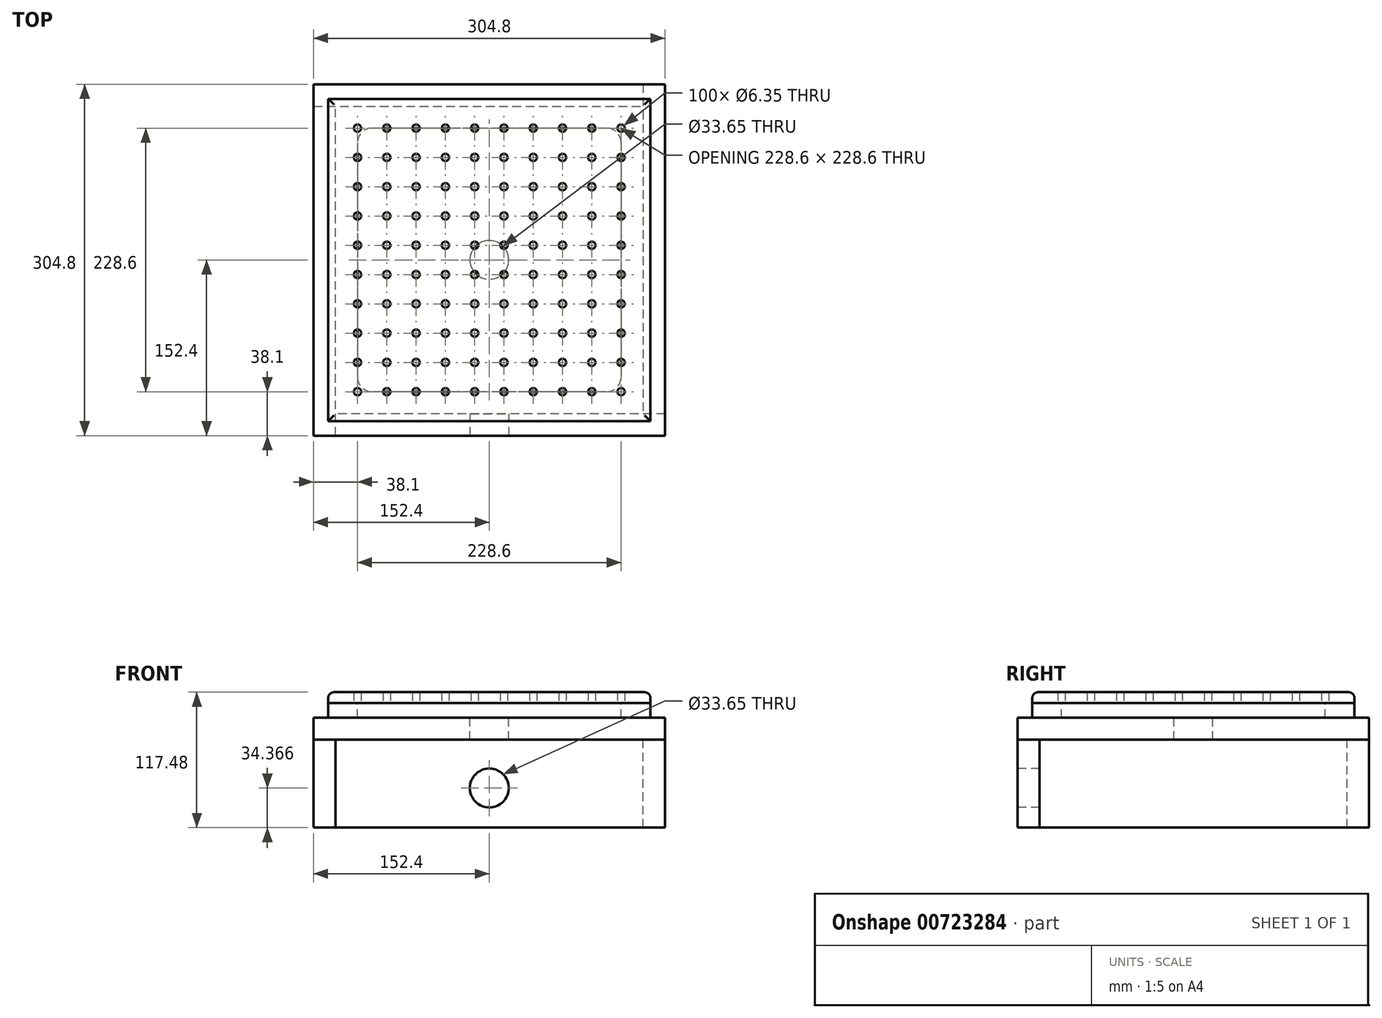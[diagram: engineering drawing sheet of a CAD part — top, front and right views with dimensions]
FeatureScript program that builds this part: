
annotation { "Feature Type Name" : "Feature", "Feature Type Description" : "" }
export const myFeature = defineFeature(function(context is Context, id is Id, definition is map)
    precondition{}
    {
        {
            var Q0;
            Q0=qCreatedBy(makeId("Top.planeOp"),FACE);
            var sketch = newSketch(context, id + "F0", { "sketchPlane" : qUnion([Q0])});
            skLineSegment(sketch, "E0.bottom", {"start": v(139.7, -139.7) * mm, "end": v(-139.7, -139.7) * mm});
            skLineSegment(sketch, "E0.top", {"start": v(139.7, 139.7) * mm, "end": v(-139.7, 139.7) * mm});
            skLineSegment(sketch, "E0.left", {"start": v(139.7, -139.7) * mm, "end": v(139.7, 139.7) * mm});
            skLineSegment(sketch, "E0.right", {"start": v(-139.7, -139.7) * mm, "end": v(-139.7, 139.7) * mm});
            skPoint(sketch, "E0.middle", {"position": v(0, 0) * mm});
            skCircle(sketch, "E1", {"center": v(-114.3, 114.3) * mm, "radius": 3.18 * mm});
            skCircle(sketch, "E2.0.1.0", {"center": v(-114.3, 88.9) * mm, "radius": 3.18 * mm});
            skCircle(sketch, "E2.0.2.0", {"center": v(-114.3, 63.5) * mm, "radius": 3.18 * mm});
            skCircle(sketch, "E2.0.3.0", {"center": v(-114.3, 38.1) * mm, "radius": 3.18 * mm});
            skCircle(sketch, "E2.0.4.0", {"center": v(-114.3, 12.7) * mm, "radius": 3.18 * mm});
            skCircle(sketch, "E2.0.5.0", {"center": v(-114.3, -12.7) * mm, "radius": 3.18 * mm});
            skCircle(sketch, "E2.0.6.0", {"center": v(-114.3, -38.1) * mm, "radius": 3.18 * mm});
            skCircle(sketch, "E2.0.7.0", {"center": v(-114.3, -63.5) * mm, "radius": 3.18 * mm});
            skCircle(sketch, "E2.0.8.0", {"center": v(-114.3, -88.9) * mm, "radius": 3.18 * mm});
            skCircle(sketch, "E2.0.9.0", {"center": v(-114.3, -114.3) * mm, "radius": 3.18 * mm});
            skCircle(sketch, "E2.1.0.0", {"center": v(-88.9, 114.3) * mm, "radius": 3.18 * mm});
            skCircle(sketch, "E2.1.1.0", {"center": v(-88.9, 88.9) * mm, "radius": 3.18 * mm});
            skCircle(sketch, "E2.1.2.0", {"center": v(-88.9, 63.5) * mm, "radius": 3.18 * mm});
            skCircle(sketch, "E2.1.3.0", {"center": v(-88.9, 38.1) * mm, "radius": 3.18 * mm});
            skCircle(sketch, "E2.1.4.0", {"center": v(-88.9, 12.7) * mm, "radius": 3.18 * mm});
            skCircle(sketch, "E2.1.5.0", {"center": v(-88.9, -12.7) * mm, "radius": 3.18 * mm});
            skCircle(sketch, "E2.1.6.0", {"center": v(-88.9, -38.1) * mm, "radius": 3.18 * mm});
            skCircle(sketch, "E2.1.7.0", {"center": v(-88.9, -63.5) * mm, "radius": 3.18 * mm});
            skCircle(sketch, "E2.1.8.0", {"center": v(-88.9, -88.9) * mm, "radius": 3.18 * mm});
            skCircle(sketch, "E2.1.9.0", {"center": v(-88.9, -114.3) * mm, "radius": 3.18 * mm});
            skCircle(sketch, "E2.2.0.0", {"center": v(-63.5, 114.3) * mm, "radius": 3.18 * mm});
            skCircle(sketch, "E2.2.1.0", {"center": v(-63.5, 88.9) * mm, "radius": 3.18 * mm});
            skCircle(sketch, "E2.2.2.0", {"center": v(-63.5, 63.5) * mm, "radius": 3.18 * mm});
            skCircle(sketch, "E2.2.3.0", {"center": v(-63.5, 38.1) * mm, "radius": 3.18 * mm});
            skCircle(sketch, "E2.2.4.0", {"center": v(-63.5, 12.7) * mm, "radius": 3.18 * mm});
            skCircle(sketch, "E2.2.5.0", {"center": v(-63.5, -12.7) * mm, "radius": 3.18 * mm});
            skCircle(sketch, "E2.2.6.0", {"center": v(-63.5, -38.1) * mm, "radius": 3.18 * mm});
            skCircle(sketch, "E2.2.7.0", {"center": v(-63.5, -63.5) * mm, "radius": 3.18 * mm});
            skCircle(sketch, "E2.2.8.0", {"center": v(-63.5, -88.9) * mm, "radius": 3.18 * mm});
            skCircle(sketch, "E2.2.9.0", {"center": v(-63.5, -114.3) * mm, "radius": 3.18 * mm});
            skCircle(sketch, "E2.3.0.0", {"center": v(-38.1, 114.3) * mm, "radius": 3.18 * mm});
            skCircle(sketch, "E2.3.1.0", {"center": v(-38.1, 88.9) * mm, "radius": 3.18 * mm});
            skCircle(sketch, "E2.3.2.0", {"center": v(-38.1, 63.5) * mm, "radius": 3.18 * mm});
            skCircle(sketch, "E2.3.3.0", {"center": v(-38.1, 38.1) * mm, "radius": 3.18 * mm});
            skCircle(sketch, "E2.3.4.0", {"center": v(-38.1, 12.7) * mm, "radius": 3.18 * mm});
            skCircle(sketch, "E2.3.5.0", {"center": v(-38.1, -12.7) * mm, "radius": 3.18 * mm});
            skCircle(sketch, "E2.3.6.0", {"center": v(-38.1, -38.1) * mm, "radius": 3.18 * mm});
            skCircle(sketch, "E2.3.7.0", {"center": v(-38.1, -63.5) * mm, "radius": 3.18 * mm});
            skCircle(sketch, "E2.3.8.0", {"center": v(-38.1, -88.9) * mm, "radius": 3.18 * mm});
            skCircle(sketch, "E2.3.9.0", {"center": v(-38.1, -114.3) * mm, "radius": 3.18 * mm});
            skCircle(sketch, "E2.4.0.0", {"center": v(-12.7, 114.3) * mm, "radius": 3.18 * mm});
            skCircle(sketch, "E2.4.1.0", {"center": v(-12.7, 88.9) * mm, "radius": 3.18 * mm});
            skCircle(sketch, "E2.4.2.0", {"center": v(-12.7, 63.5) * mm, "radius": 3.18 * mm});
            skCircle(sketch, "E2.4.3.0", {"center": v(-12.7, 38.1) * mm, "radius": 3.18 * mm});
            skCircle(sketch, "E2.4.4.0", {"center": v(-12.7, 12.7) * mm, "radius": 3.18 * mm});
            skCircle(sketch, "E2.4.5.0", {"center": v(-12.7, -12.7) * mm, "radius": 3.18 * mm});
            skCircle(sketch, "E2.4.6.0", {"center": v(-12.7, -38.1) * mm, "radius": 3.18 * mm});
            skCircle(sketch, "E2.4.7.0", {"center": v(-12.7, -63.5) * mm, "radius": 3.18 * mm});
            skCircle(sketch, "E2.4.8.0", {"center": v(-12.7, -88.9) * mm, "radius": 3.18 * mm});
            skCircle(sketch, "E2.4.9.0", {"center": v(-12.7, -114.3) * mm, "radius": 3.18 * mm});
            skCircle(sketch, "E2.5.0.0", {"center": v(12.7, 114.3) * mm, "radius": 3.18 * mm});
            skCircle(sketch, "E2.5.1.0", {"center": v(12.7, 88.9) * mm, "radius": 3.18 * mm});
            skCircle(sketch, "E2.5.2.0", {"center": v(12.7, 63.5) * mm, "radius": 3.18 * mm});
            skCircle(sketch, "E2.5.3.0", {"center": v(12.7, 38.1) * mm, "radius": 3.18 * mm});
            skCircle(sketch, "E2.5.4.0", {"center": v(12.7, 12.7) * mm, "radius": 3.18 * mm});
            skCircle(sketch, "E2.5.5.0", {"center": v(12.7, -12.7) * mm, "radius": 3.18 * mm});
            skCircle(sketch, "E2.5.6.0", {"center": v(12.7, -38.1) * mm, "radius": 3.18 * mm});
            skCircle(sketch, "E2.5.7.0", {"center": v(12.7, -63.5) * mm, "radius": 3.18 * mm});
            skCircle(sketch, "E2.5.8.0", {"center": v(12.7, -88.9) * mm, "radius": 3.18 * mm});
            skCircle(sketch, "E2.5.9.0", {"center": v(12.7, -114.3) * mm, "radius": 3.18 * mm});
            skCircle(sketch, "E2.6.0.0", {"center": v(38.1, 114.3) * mm, "radius": 3.18 * mm});
            skCircle(sketch, "E2.6.1.0", {"center": v(38.1, 88.9) * mm, "radius": 3.18 * mm});
            skCircle(sketch, "E2.6.2.0", {"center": v(38.1, 63.5) * mm, "radius": 3.18 * mm});
            skCircle(sketch, "E2.6.3.0", {"center": v(38.1, 38.1) * mm, "radius": 3.18 * mm});
            skCircle(sketch, "E2.6.4.0", {"center": v(38.1, 12.7) * mm, "radius": 3.18 * mm});
            skCircle(sketch, "E2.6.5.0", {"center": v(38.1, -12.7) * mm, "radius": 3.18 * mm});
            skCircle(sketch, "E2.6.6.0", {"center": v(38.1, -38.1) * mm, "radius": 3.18 * mm});
            skCircle(sketch, "E2.6.7.0", {"center": v(38.1, -63.5) * mm, "radius": 3.18 * mm});
            skCircle(sketch, "E2.6.8.0", {"center": v(38.1, -88.9) * mm, "radius": 3.18 * mm});
            skCircle(sketch, "E2.6.9.0", {"center": v(38.1, -114.3) * mm, "radius": 3.18 * mm});
            skCircle(sketch, "E2.7.0.0", {"center": v(63.5, 114.3) * mm, "radius": 3.18 * mm});
            skCircle(sketch, "E2.7.1.0", {"center": v(63.5, 88.9) * mm, "radius": 3.18 * mm});
            skCircle(sketch, "E2.7.2.0", {"center": v(63.5, 63.5) * mm, "radius": 3.18 * mm});
            skCircle(sketch, "E2.7.3.0", {"center": v(63.5, 38.1) * mm, "radius": 3.18 * mm});
            skCircle(sketch, "E2.7.4.0", {"center": v(63.5, 12.7) * mm, "radius": 3.18 * mm});
            skCircle(sketch, "E2.7.5.0", {"center": v(63.5, -12.7) * mm, "radius": 3.18 * mm});
            skCircle(sketch, "E2.7.6.0", {"center": v(63.5, -38.1) * mm, "radius": 3.18 * mm});
            skCircle(sketch, "E2.7.7.0", {"center": v(63.5, -63.5) * mm, "radius": 3.18 * mm});
            skCircle(sketch, "E2.7.8.0", {"center": v(63.5, -88.9) * mm, "radius": 3.18 * mm});
            skCircle(sketch, "E2.7.9.0", {"center": v(63.5, -114.3) * mm, "radius": 3.18 * mm});
            skCircle(sketch, "E2.8.0.0", {"center": v(88.9, 114.3) * mm, "radius": 3.18 * mm});
            skCircle(sketch, "E2.8.1.0", {"center": v(88.9, 88.9) * mm, "radius": 3.18 * mm});
            skCircle(sketch, "E2.8.2.0", {"center": v(88.9, 63.5) * mm, "radius": 3.18 * mm});
            skCircle(sketch, "E2.8.3.0", {"center": v(88.9, 38.1) * mm, "radius": 3.18 * mm});
            skCircle(sketch, "E2.8.4.0", {"center": v(88.9, 12.7) * mm, "radius": 3.18 * mm});
            skCircle(sketch, "E2.8.5.0", {"center": v(88.9, -12.7) * mm, "radius": 3.18 * mm});
            skCircle(sketch, "E2.8.6.0", {"center": v(88.9, -38.1) * mm, "radius": 3.18 * mm});
            skCircle(sketch, "E2.8.7.0", {"center": v(88.9, -63.5) * mm, "radius": 3.18 * mm});
            skCircle(sketch, "E2.8.8.0", {"center": v(88.9, -88.9) * mm, "radius": 3.18 * mm});
            skCircle(sketch, "E2.8.9.0", {"center": v(88.9, -114.3) * mm, "radius": 3.18 * mm});
            skCircle(sketch, "E2.9.0.0", {"center": v(114.3, 114.3) * mm, "radius": 3.18 * mm});
            skCircle(sketch, "E2.9.1.0", {"center": v(114.3, 88.9) * mm, "radius": 3.18 * mm});
            skCircle(sketch, "E2.9.2.0", {"center": v(114.3, 63.5) * mm, "radius": 3.18 * mm});
            skCircle(sketch, "E2.9.3.0", {"center": v(114.3, 38.1) * mm, "radius": 3.18 * mm});
            skCircle(sketch, "E2.9.4.0", {"center": v(114.3, 12.7) * mm, "radius": 3.18 * mm});
            skCircle(sketch, "E2.9.5.0", {"center": v(114.3, -12.7) * mm, "radius": 3.18 * mm});
            skCircle(sketch, "E2.9.6.0", {"center": v(114.3, -38.1) * mm, "radius": 3.18 * mm});
            skCircle(sketch, "E2.9.7.0", {"center": v(114.3, -63.5) * mm, "radius": 3.18 * mm});
            skCircle(sketch, "E2.9.8.0", {"center": v(114.3, -88.9) * mm, "radius": 3.18 * mm});
            skCircle(sketch, "E2.9.9.0", {"center": v(114.3, -114.3) * mm, "radius": 3.18 * mm});
            skLineSegment(sketch, "E2.direction1", {"start": v(-114.3, 114.3) * mm, "end": v(-88.9, 114.3) * mm, "construction": true});
            skLineSegment(sketch, "E2.direction2", {"start": v(-114.3, 114.3) * mm, "end": v(-114.3, 88.9) * mm, "construction": true});
            skSolve(sketch);
        }
        {
            var Q0;
            Q0=makeQuery(id+"F0.imprint","IMPRINT",FACE,{"disambiguationData":[TD([[makeQuery(id+"F0.imprint","IMPRINT",EDGE,{"derivedFrom":sQuery(id+"F0.wireOp",EDGE,"E0.bottom")}),-1.0]])]});
            extrude(context, id + "F1", {"entities" : qUnion([Q0]), "depth" : 9.52 * mm, "offsetDistance" : 25.4 * mm});
        }
        {
            var Q0;
            Q0=makeQuery(id+"F1.opExtrude","CAP_EDGE",EDGE,{"disambiguationData":[OSD([sQuery(id+"F0.wireOp",EDGE,"E0.right")])],"isStart":false});
            var Q1;
            Q1=makeQuery(id+"F1.opExtrude","CAP_EDGE",EDGE,{"disambiguationData":[OSD([sQuery(id+"F0.wireOp",EDGE,"E0.left")])],"isStart":false});
            var Q2;
            Q2=makeQuery(id+"F1.opExtrude","CAP_EDGE",EDGE,{"disambiguationData":[OSD([sQuery(id+"F0.wireOp",EDGE,"E0.top")])],"isStart":false});
            var Q3;
            Q3=makeQuery(id+"F1.opExtrude","CAP_EDGE",EDGE,{"disambiguationData":[OSD([sQuery(id+"F0.wireOp",EDGE,"E0.bottom")])],"isStart":false});
            fillet(context, id + "F2", {"entities" : qUnion([Q0, Q1, Q2, Q3]), "radius" : 5.08 * mm, "tangentPropagation" : true, "allowEdgeOverflow" : false});
        }
        {
            var Q0;
            Q0=makeQuery(id+"F1.opExtrude","CAP_FACE",FACE,{"disambiguationData":[OSD([sQuery(id+"F0.wireOp",EDGE,"E0.bottom"),sQuery(id+"F0.wireOp",EDGE,"E0.top"),sQuery(id+"F0.wireOp",EDGE,"E0.left"),sQuery(id+"F0.wireOp",EDGE,"E0.right"),sQuery(id+"F0.wireOp",EDGE,"E1"),sQuery(id+"F0.wireOp",EDGE,"E2.0.1.0"),sQuery(id+"F0.wireOp",EDGE,"E2.0.2.0"),sQuery(id+"F0.wireOp",EDGE,"E2.0.3.0"),sQuery(id+"F0.wireOp",EDGE,"E2.0.4.0"),sQuery(id+"F0.wireOp",EDGE,"E2.0.5.0"),sQuery(id+"F0.wireOp",EDGE,"E2.0.6.0"),sQuery(id+"F0.wireOp",EDGE,"E2.0.7.0"),sQuery(id+"F0.wireOp",EDGE,"E2.0.8.0"),sQuery(id+"F0.wireOp",EDGE,"E2.0.9.0"),sQuery(id+"F0.wireOp",EDGE,"E2.0.10.0"),sQuery(id+"F0.wireOp",EDGE,"E2.1.0.0"),sQuery(id+"F0.wireOp",EDGE,"E2.1.1.0"),sQuery(id+"F0.wireOp",EDGE,"E2.1.2.0"),sQuery(id+"F0.wireOp",EDGE,"E2.1.3.0"),sQuery(id+"F0.wireOp",EDGE,"E2.1.4.0"),sQuery(id+"F0.wireOp",EDGE,"E2.1.5.0"),sQuery(id+"F0.wireOp",EDGE,"E2.1.6.0"),sQuery(id+"F0.wireOp",EDGE,"E2.1.7.0"),sQuery(id+"F0.wireOp",EDGE,"E2.1.8.0"),sQuery(id+"F0.wireOp",EDGE,"E2.1.9.0"),sQuery(id+"F0.wireOp",EDGE,"E2.1.10.0"),sQuery(id+"F0.wireOp",EDGE,"E2.2.0.0"),sQuery(id+"F0.wireOp",EDGE,"E2.2.1.0"),sQuery(id+"F0.wireOp",EDGE,"E2.2.2.0"),sQuery(id+"F0.wireOp",EDGE,"E2.2.3.0"),sQuery(id+"F0.wireOp",EDGE,"E2.2.4.0"),sQuery(id+"F0.wireOp",EDGE,"E2.2.5.0"),sQuery(id+"F0.wireOp",EDGE,"E2.2.6.0"),sQuery(id+"F0.wireOp",EDGE,"E2.2.7.0"),sQuery(id+"F0.wireOp",EDGE,"E2.2.8.0"),sQuery(id+"F0.wireOp",EDGE,"E2.2.9.0"),sQuery(id+"F0.wireOp",EDGE,"E2.2.10.0"),sQuery(id+"F0.wireOp",EDGE,"E2.3.0.0"),sQuery(id+"F0.wireOp",EDGE,"E2.3.1.0"),sQuery(id+"F0.wireOp",EDGE,"E2.3.2.0"),sQuery(id+"F0.wireOp",EDGE,"E2.3.3.0"),sQuery(id+"F0.wireOp",EDGE,"E2.3.4.0"),sQuery(id+"F0.wireOp",EDGE,"E2.3.5.0"),sQuery(id+"F0.wireOp",EDGE,"E2.3.6.0"),sQuery(id+"F0.wireOp",EDGE,"E2.3.7.0"),sQuery(id+"F0.wireOp",EDGE,"E2.3.8.0"),sQuery(id+"F0.wireOp",EDGE,"E2.3.9.0"),sQuery(id+"F0.wireOp",EDGE,"E2.3.10.0"),sQuery(id+"F0.wireOp",EDGE,"E2.4.0.0"),sQuery(id+"F0.wireOp",EDGE,"E2.4.1.0"),sQuery(id+"F0.wireOp",EDGE,"E2.4.2.0"),sQuery(id+"F0.wireOp",EDGE,"E2.4.3.0"),sQuery(id+"F0.wireOp",EDGE,"E2.4.4.0"),sQuery(id+"F0.wireOp",EDGE,"E2.4.5.0"),sQuery(id+"F0.wireOp",EDGE,"E2.4.6.0"),sQuery(id+"F0.wireOp",EDGE,"E2.4.7.0"),sQuery(id+"F0.wireOp",EDGE,"E2.4.8.0"),sQuery(id+"F0.wireOp",EDGE,"E2.4.9.0"),sQuery(id+"F0.wireOp",EDGE,"E2.4.10.0"),sQuery(id+"F0.wireOp",EDGE,"E2.5.0.0"),sQuery(id+"F0.wireOp",EDGE,"E2.5.1.0"),sQuery(id+"F0.wireOp",EDGE,"E2.5.2.0"),sQuery(id+"F0.wireOp",EDGE,"E2.5.3.0"),sQuery(id+"F0.wireOp",EDGE,"E2.5.4.0"),sQuery(id+"F0.wireOp",EDGE,"E2.5.5.0"),sQuery(id+"F0.wireOp",EDGE,"E2.5.6.0"),sQuery(id+"F0.wireOp",EDGE,"E2.5.7.0"),sQuery(id+"F0.wireOp",EDGE,"E2.5.8.0"),sQuery(id+"F0.wireOp",EDGE,"E2.5.9.0"),sQuery(id+"F0.wireOp",EDGE,"E2.5.10.0"),sQuery(id+"F0.wireOp",EDGE,"E2.6.0.0"),sQuery(id+"F0.wireOp",EDGE,"E2.6.1.0"),sQuery(id+"F0.wireOp",EDGE,"E2.6.2.0"),sQuery(id+"F0.wireOp",EDGE,"E2.6.3.0"),sQuery(id+"F0.wireOp",EDGE,"E2.6.4.0"),sQuery(id+"F0.wireOp",EDGE,"E2.6.5.0"),sQuery(id+"F0.wireOp",EDGE,"E2.6.6.0"),sQuery(id+"F0.wireOp",EDGE,"E2.6.7.0"),sQuery(id+"F0.wireOp",EDGE,"E2.6.8.0"),sQuery(id+"F0.wireOp",EDGE,"E2.6.9.0"),sQuery(id+"F0.wireOp",EDGE,"E2.6.10.0"),sQuery(id+"F0.wireOp",EDGE,"E2.7.0.0"),sQuery(id+"F0.wireOp",EDGE,"E2.7.1.0"),sQuery(id+"F0.wireOp",EDGE,"E2.7.2.0"),sQuery(id+"F0.wireOp",EDGE,"E2.7.3.0"),sQuery(id+"F0.wireOp",EDGE,"E2.7.4.0"),sQuery(id+"F0.wireOp",EDGE,"E2.7.5.0"),sQuery(id+"F0.wireOp",EDGE,"E2.7.6.0"),sQuery(id+"F0.wireOp",EDGE,"E2.7.7.0"),sQuery(id+"F0.wireOp",EDGE,"E2.7.8.0"),sQuery(id+"F0.wireOp",EDGE,"E2.7.9.0"),sQuery(id+"F0.wireOp",EDGE,"E2.7.10.0"),sQuery(id+"F0.wireOp",EDGE,"E2.8.0.0"),sQuery(id+"F0.wireOp",EDGE,"E2.8.1.0"),sQuery(id+"F0.wireOp",EDGE,"E2.8.2.0"),sQuery(id+"F0.wireOp",EDGE,"E2.8.3.0"),sQuery(id+"F0.wireOp",EDGE,"E2.8.4.0"),sQuery(id+"F0.wireOp",EDGE,"E2.8.5.0"),sQuery(id+"F0.wireOp",EDGE,"E2.8.6.0"),sQuery(id+"F0.wireOp",EDGE,"E2.8.7.0"),sQuery(id+"F0.wireOp",EDGE,"E2.8.8.0"),sQuery(id+"F0.wireOp",EDGE,"E2.8.9.0"),sQuery(id+"F0.wireOp",EDGE,"E2.8.10.0"),sQuery(id+"F0.wireOp",EDGE,"E2.9.0.0"),sQuery(id+"F0.wireOp",EDGE,"E2.9.1.0"),sQuery(id+"F0.wireOp",EDGE,"E2.9.2.0"),sQuery(id+"F0.wireOp",EDGE,"E2.9.3.0"),sQuery(id+"F0.wireOp",EDGE,"E2.9.4.0"),sQuery(id+"F0.wireOp",EDGE,"E2.9.5.0"),sQuery(id+"F0.wireOp",EDGE,"E2.9.6.0"),sQuery(id+"F0.wireOp",EDGE,"E2.9.7.0"),sQuery(id+"F0.wireOp",EDGE,"E2.9.8.0"),sQuery(id+"F0.wireOp",EDGE,"E2.9.9.0"),sQuery(id+"F0.wireOp",EDGE,"E2.9.10.0"),sQuery(id+"F0.wireOp",EDGE,"E2.10.0.0"),sQuery(id+"F0.wireOp",EDGE,"E2.10.1.0"),sQuery(id+"F0.wireOp",EDGE,"E2.10.2.0"),sQuery(id+"F0.wireOp",EDGE,"E2.10.3.0"),sQuery(id+"F0.wireOp",EDGE,"E2.10.4.0"),sQuery(id+"F0.wireOp",EDGE,"E2.10.5.0"),sQuery(id+"F0.wireOp",EDGE,"E2.10.6.0"),sQuery(id+"F0.wireOp",EDGE,"E2.10.7.0"),sQuery(id+"F0.wireOp",EDGE,"E2.10.8.0"),sQuery(id+"F0.wireOp",EDGE,"E2.10.9.0"),sQuery(id+"F0.wireOp",EDGE,"E2.10.10.0")])],"isStart":true});
            var sketch = newSketch(context, id + "F3", { "sketchPlane" : qUnion([Q0])});
            skLineSegment(sketch, "E3.bottom", {"start": v(-139.7, 139.7) * mm, "end": v(139.7, 139.7) * mm});
            skLineSegment(sketch, "E3.top", {"start": v(-139.7, -139.7) * mm, "end": v(139.7, -139.7) * mm});
            skLineSegment(sketch, "E3.left", {"start": v(-139.7, 139.7) * mm, "end": v(-139.7, -139.7) * mm});
            skLineSegment(sketch, "E3.right", {"start": v(139.7, 139.7) * mm, "end": v(139.7, -139.7) * mm});
            skLineSegment(sketch, "E4.bottom", {"start": v(114.3, -114.3) * mm, "end": v(-114.3, -114.3) * mm});
            skLineSegment(sketch, "E4.top", {"start": v(114.3, 114.3) * mm, "end": v(-114.3, 114.3) * mm});
            skLineSegment(sketch, "E4.left", {"start": v(114.3, -114.3) * mm, "end": v(114.3, 114.3) * mm});
            skLineSegment(sketch, "E4.right", {"start": v(-114.3, -114.3) * mm, "end": v(-114.3, 114.3) * mm});
            skPoint(sketch, "E4.middle", {"position": v(0, 0) * mm});
            skSolve(sketch);
        }
        {
            var Q0;
            Q0 = qSketchRegion(id + "F3", true);
            extrude(context, id + "F4", {"entities" : qUnion([Q0]), "depth" : 12.7 * mm, "offsetDistance" : 25.4 * mm});
        }
        {
            var Q0;
            Q0=makeQuery(id+"F4.opExtrude","SWEPT_EDGE",EDGE,{"disambiguationData":[OSD([sQuery(id+"F3.wireOp",EDGE,"E4.top"),sQuery(id+"F3.wireOp",EDGE,"E4.right")])]});
            var Q1;
            Q1=makeQuery(id+"F4.opExtrude","SWEPT_EDGE",EDGE,{"disambiguationData":[OSD([sQuery(id+"F3.wireOp",EDGE,"E4.top"),sQuery(id+"F3.wireOp",EDGE,"E4.left")])]});
            var Q2;
            Q2=makeQuery(id+"F4.opExtrude","SWEPT_EDGE",EDGE,{"disambiguationData":[OSD([sQuery(id+"F3.wireOp",EDGE,"E4.bottom"),sQuery(id+"F3.wireOp",EDGE,"E4.left")])]});
            var Q3;
            Q3=makeQuery(id+"F4.opExtrude","SWEPT_EDGE",EDGE,{"disambiguationData":[OSD([sQuery(id+"F3.wireOp",EDGE,"E4.bottom"),sQuery(id+"F3.wireOp",EDGE,"E4.right")])]});
            fillet(context, id + "F5", {"entities" : qUnion([Q0, Q1, Q2, Q3]), "radius" : 12.7 * mm, "tangentPropagation" : true, "allowEdgeOverflow" : false});
        }
        {
            var Q0;
            Q0=makeQuery(id+"F4.opExtrude","CAP_FACE",FACE,{"disambiguationData":[OSD([sQuery(id+"F3.wireOp",EDGE,"E3.bottom"),sQuery(id+"F3.wireOp",EDGE,"E3.top"),sQuery(id+"F3.wireOp",EDGE,"E3.left"),sQuery(id+"F3.wireOp",EDGE,"E3.right"),sQuery(id+"F3.wireOp",EDGE,"E4.bottom"),sQuery(id+"F3.wireOp",EDGE,"E4.top"),sQuery(id+"F3.wireOp",EDGE,"E4.left"),sQuery(id+"F3.wireOp",EDGE,"E4.right")])],"isStart":false});
            var sketch = newSketch(context, id + "F6", { "sketchPlane" : qUnion([Q0])});
            skLineSegment(sketch, "E5.bottom", {"start": v(152.4, -152.4) * mm, "end": v(-152.4, -152.4) * mm});
            skLineSegment(sketch, "E5.top", {"start": v(152.4, 152.4) * mm, "end": v(-152.4, 152.4) * mm});
            skLineSegment(sketch, "E5.left", {"start": v(152.4, -152.4) * mm, "end": v(152.4, 152.4) * mm});
            skLineSegment(sketch, "E5.right", {"start": v(-152.4, -152.4) * mm, "end": v(-152.4, 152.4) * mm});
            skPoint(sketch, "E5.middle", {"position": v(0, 0) * mm});
            skCircle(sketch, "E6", {"center": v(0, 0) * mm, "radius": 16.83 * mm});
            skSolve(sketch);
        }
        {
            var Q0;
            Q0 = qSketchRegion(id + "F6", true);
            extrude(context, id + "F7", {"entities" : qUnion([Q0]), "depth" : 19.05 * mm, "offsetDistance" : 25.4 * mm});
        }
        {
            var Q0;
            Q0=makeQuery(id+"F7.opExtrude","CAP_FACE",FACE,{"disambiguationData":[OSD([sQuery(id+"F6.wireOp",EDGE,"E5.bottom"),sQuery(id+"F6.wireOp",EDGE,"E5.top"),sQuery(id+"F6.wireOp",EDGE,"E5.left"),sQuery(id+"F6.wireOp",EDGE,"E5.right"),sQuery(id+"F6.wireOp",EDGE,"E6")])],"isStart":false});
            var sketch = newSketch(context, id + "F8", { "sketchPlane" : qUnion([Q0])});
            skLineSegment(sketch, "E7.bottom", {"start": v(-152.4, 152.4) * mm, "end": v(-133.35, 152.4) * mm});
            skLineSegment(sketch, "E7.top", {"start": v(-152.4, -133.35) * mm, "end": v(-133.35, -133.35) * mm});
            skLineSegment(sketch, "E7.left", {"start": v(-152.4, 152.4) * mm, "end": v(-152.4, -133.35) * mm});
            skLineSegment(sketch, "E7.right", {"start": v(-133.35, 152.4) * mm, "end": v(-133.35, -133.35) * mm});
            skSolve(sketch);
        }
        {
            var Q0;
            Q0=makeQuery(id+"F8.imprint","IMPRINT",FACE,{"disambiguationData":[TD([[makeQuery(id+"F8.imprint","IMPRINT",EDGE,{"derivedFrom":sQuery(id+"F8.wireOp",EDGE,"E7.bottom")}),1.0]])]});
            extrude(context, id + "F9", {"entities" : qUnion([Q0]), "depth" : 76.2 * mm, "offsetDistance" : 25.4 * mm});
        }
        {
            var Q0;
            Q0=makeQuery(id+"F9.opExtrude","SWEPT_BODY",BODY,{"disambiguationData":[OSD([sQuery(id+"F8.wireOp",EDGE,"E7.bottom"),sQuery(id+"F8.wireOp",EDGE,"E7.top"),sQuery(id+"F8.wireOp",EDGE,"E7.left"),sQuery(id+"F8.wireOp",EDGE,"E7.right")])]});
            var Q1;
            Q1=makeQuery(id+"F7.opExtrude","CAP_EDGE",EDGE,{"disambiguationData":[OSD([sQuery(id+"F6.wireOp",EDGE,"E6")])],"isStart":false});
            circularPattern(context, id + "F10", {"entities" : qUnion([Q0]), "axis" : qUnion([Q1]), "angle" : 360 * degree, "instanceCount" : 4, "equalSpace" : true});
        }
        {
            var Q0;
            Q0=makeQuery(id+"F10.opPattern","COPY",FACE,{"derivedFrom":makeQuery(id+"F9.opExtrude","SWEPT_FACE",FACE,{"disambiguationData":[OSD([sQuery(id+"F8.wireOp",EDGE,"E7.left")])]}),"instanceName":"3"});
            var sketch = newSketch(context, id + "F11", { "sketchPlane" : qUnion([Q0])});
            skCircle(sketch, "E8", {"center": v(0, -73.58) * mm, "radius": 16.83 * mm});
            skSolve(sketch);
        }
        {
            var Q0;
            Q0=makeQuery(id+"F11.imprint","IMPRINT",FACE,{"disambiguationData":[TD([[makeQuery(id+"F11.imprint","IMPRINT",EDGE,{"derivedFrom":sQuery(id+"F11.wireOp",EDGE,"E8")}),1.0]])]});
            extrude(context, id + "F12", {"entities" : qUnion([Q0]), "operationType" : NewBodyOperationType.REMOVE, "oppositeDirection" : true, "depth" : 25.4 * mm, "offsetDistance" : 25.4 * mm});
        }
    });
